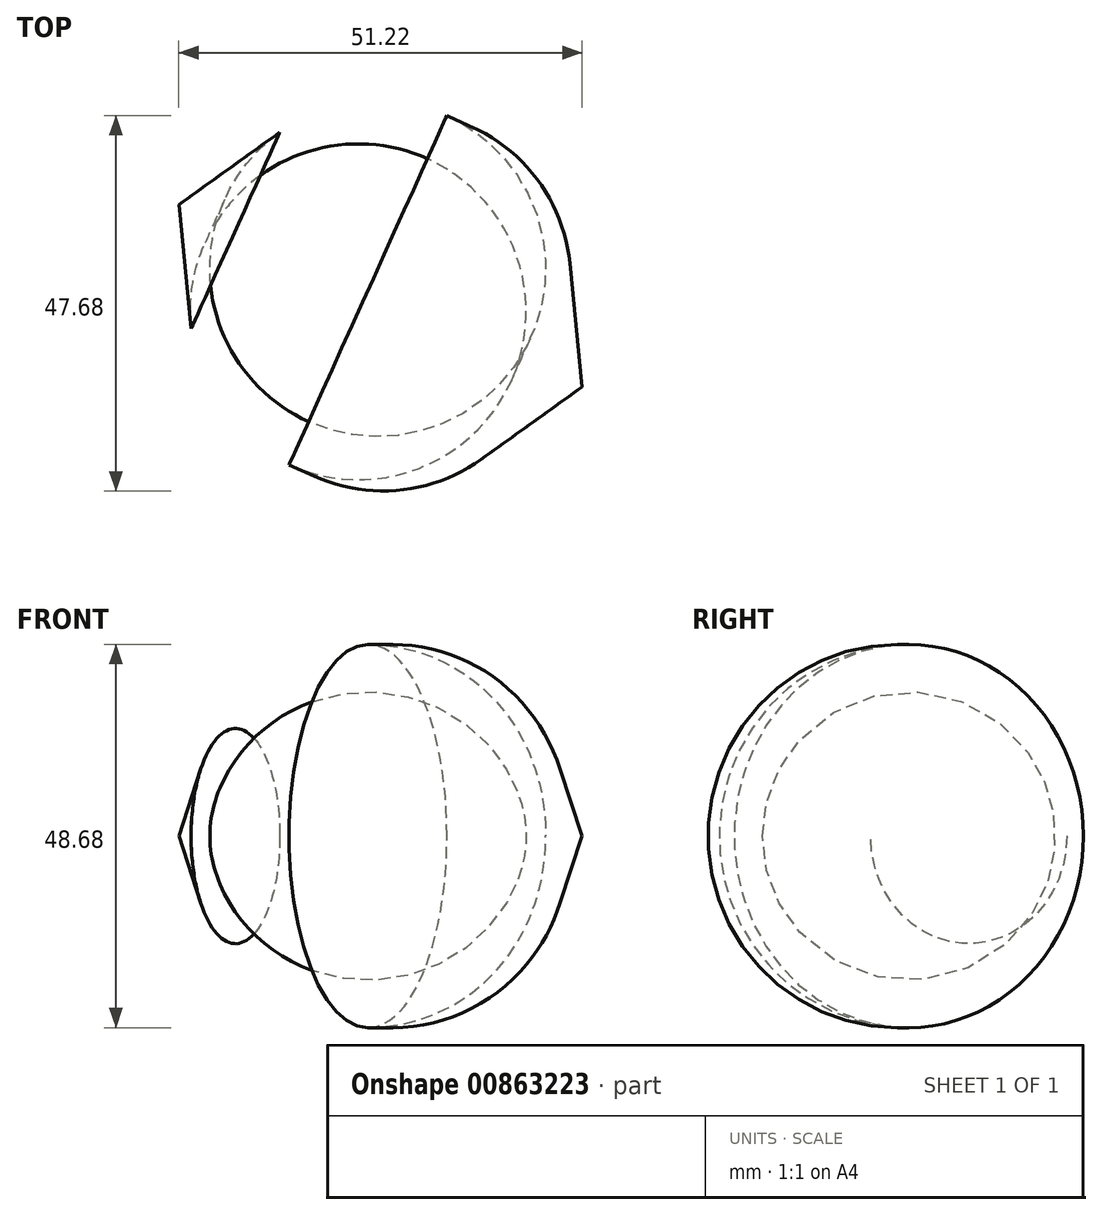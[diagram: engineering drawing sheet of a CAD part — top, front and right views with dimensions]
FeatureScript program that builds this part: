
annotation { "Feature Type Name" : "Feature", "Feature Type Description" : "" }
export const myFeature = defineFeature(function(context is Context, id is Id, definition is map)
    precondition{}
    {
        {
            var Q0;
            Q0=qCreatedBy(makeId("Top.planeOp"),FACE);
            var sketch = newSketch(context, id + "F0", { "sketchPlane" : qUnion([Q0])});
            skLineSegment(sketch, "E0.2", {"start": v(25.6, -11.58) * mm, "end": v(2.78, -27.96) * mm});
            skLineSegment(sketch, "E0.3", {"start": v(2.78, -27.96) * mm, "end": v(-22.83, -16.39) * mm});
            skLineSegment(sketch, "E0.4", {"start": v(-22.83, -16.39) * mm, "end": v(-25.6, 11.58) * mm});
            skPoint(sketch, "E0.0.midPoint", {"position": v(10.02, 22.18) * mm});
            skPoint(sketch, "E1.orphan", {"position": v(-2.78, 27.96) * mm});
            skPoint(sketch, "E2.orphan", {"position": v(22.83, 16.39) * mm});
            skLineSegment(sketch, "E3", {"start": v(-25.6, 11.58) * mm, "end": v(25.6, -11.58) * mm});
            skSolve(sketch);
        }
        {
            var Q0;
            Q0=makeQuery(id+"F0.imprint","IMPRINT",FACE,{"disambiguationData":[TD([[makeQuery(id+"F0.imprint","IMPRINT",EDGE,{"derivedFrom":sQuery(id+"F0.wireOp",EDGE,"E0.2")}),-1.0]])]});
            var Q1;
            Q1=sQuery(id+"F0.wireOp",EDGE,"E3");
            revolve(context, id + "F1", {"surfaceOperationType" : NewSurfaceOperationType.NEW, "entities" : qUnion([Q0]), "axis" : qUnion([Q1]), "revolveType" : RevolveType.FULL});
        }
        {
            var Q0;
            Q0=makeQuery(id+"F1.opRevolve","SWEPT_EDGE",EDGE,{"disambiguationData":[OSD([sQuery(id+"F0.wireOp",EDGE,"E0.2"),sQuery(id+"F0.wireOp",EDGE,"E0.3")])]});
            var Q1;
            Q1=makeQuery(id+"F1.opRevolve","SWEPT_EDGE",EDGE,{"disambiguationData":[OSD([sQuery(id+"F0.wireOp",EDGE,"E0.3"),sQuery(id+"F0.wireOp",EDGE,"E0.4")])]});
            fillet(context, id + "F2", {"entities" : qUnion([Q0, Q1]), "radius" : 21.33 * mm, "tangentPropagation" : true, "allowEdgeOverflow" : false});
        }
    });
